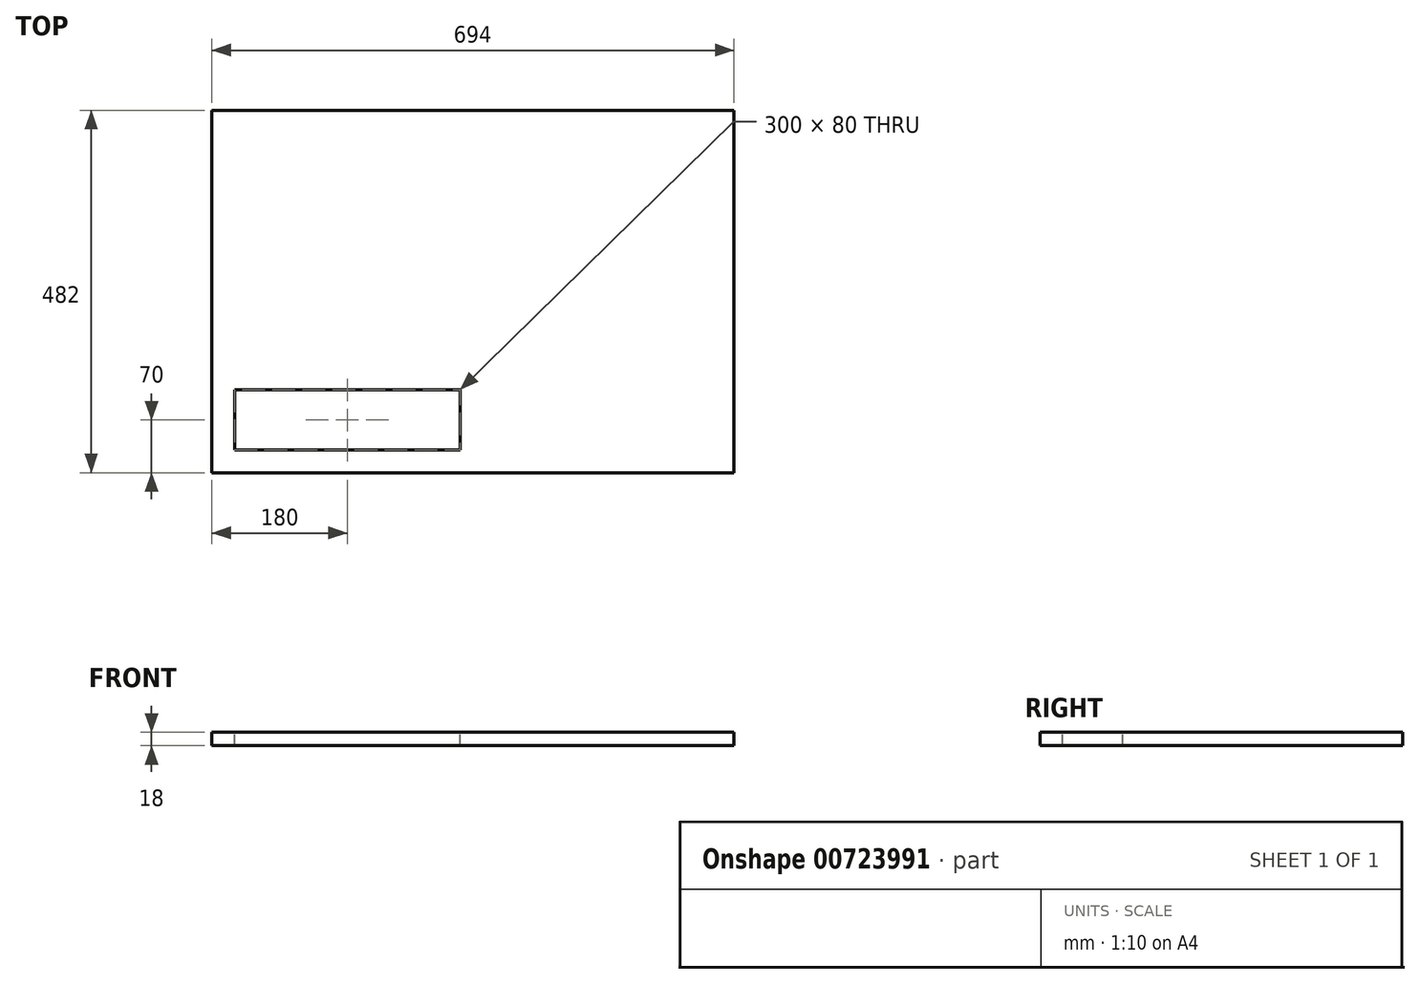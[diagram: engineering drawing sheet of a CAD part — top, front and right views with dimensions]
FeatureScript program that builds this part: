
annotation { "Feature Type Name" : "Feature", "Feature Type Description" : "" }
export const myFeature = defineFeature(function(context is Context, id is Id, definition is map)
    precondition{}
    {
        {
            var Q0;
            Q0=qCreatedBy(makeId("Top.planeOp"),FACE);
            var sketch = newSketch(context, id + "F0", { "sketchPlane" : qUnion([Q0])});
            skLineSegment(sketch, "E0.bottom", {"start": v(-347, 241) * mm, "end": v(347, 241) * mm});
            skLineSegment(sketch, "E0.top", {"start": v(-347, -241) * mm, "end": v(347, -241) * mm});
            skLineSegment(sketch, "E0.left", {"start": v(-347, 241) * mm, "end": v(-347, -241) * mm});
            skLineSegment(sketch, "E0.right", {"start": v(347, 241) * mm, "end": v(347, -241) * mm});
            skLineSegment(sketch, "E1", {"start": v(-347, 241) * mm, "end": v(347, -241) * mm, "construction": true});
            skLineSegment(sketch, "E2", {"start": v(347, 241) * mm, "end": v(-347, -241) * mm, "construction": true});
            skSolve(sketch);
        }
        {
            var Q0;
            Q0=qSketchRegion(id+"F0",true);
            extrude(context, id + "F1", {"entities" : qUnion([Q0]), "depth" : 18 * mm, "offsetDistance" : 25 * mm});
        }
        {
            var Q0;
            Q0=makeQuery(id+"F1.opExtrude","CAP_FACE",FACE,{"disambiguationData":[OSD([sQuery(id+"F0.wireOp",EDGE,"E0.bottom"),sQuery(id+"F0.wireOp",EDGE,"E0.top"),sQuery(id+"F0.wireOp",EDGE,"E0.left"),sQuery(id+"F0.wireOp",EDGE,"E0.right")])],"isStart":false});
            var sketch = newSketch(context, id + "F2", { "sketchPlane" : qUnion([Q0])});
            skLineSegment(sketch, "E3.bottom", {"start": v(-317, -131) * mm, "end": v(-17, -131) * mm});
            skLineSegment(sketch, "E3.top", {"start": v(-317, -211) * mm, "end": v(-17, -211) * mm});
            skLineSegment(sketch, "E3.left", {"start": v(-317, -131) * mm, "end": v(-317, -211) * mm});
            skLineSegment(sketch, "E3.right", {"start": v(-17, -131) * mm, "end": v(-17, -211) * mm});
            skLineSegment(sketch, "E4", {"start": v(-167, -211) * mm, "end": v(-167, -241) * mm, "construction": true});
            skLineSegment(sketch, "E5", {"start": v(-317, -171) * mm, "end": v(-347, -171) * mm, "construction": true});
            skSolve(sketch);
        }
        {
            var Q0;
            Q0=qSketchRegion(id+"F2",true);
            extrude(context, id + "F3", {"entities" : qUnion([Q0]), "operationType" : NewBodyOperationType.REMOVE, "oppositeDirection" : true, "depth" : 18 * mm, "offsetDistance" : 25 * mm});
        }
    });
